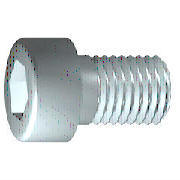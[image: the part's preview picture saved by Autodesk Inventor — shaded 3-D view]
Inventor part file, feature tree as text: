
AUTODESK INVENTOR PART (.ipt)
format: ipt  version: 2020 (Build 240168000, 168)  size: 196,608 bytes
history: native  units: mm (DEFAULTED — no unit token found)
features: sketch x2, other x1, extrude x1, plane x1, fillet x1
ambient origin geometry x7: Origin, YZ Plane, XY Plane, X Axis, Y Axis, Z Axis, Center Point
bodies: Solid1 (feature_tree)
feature tree (6):
  other  "Bryła"
  extrude  "Szczelina"  Depth=13.6mm
  plane  "Work Plane1"
  fillet  "Fillet2"  Radius=0.49086mm
  sketch  "Szkic1"
  sketch  "Szkic2"
